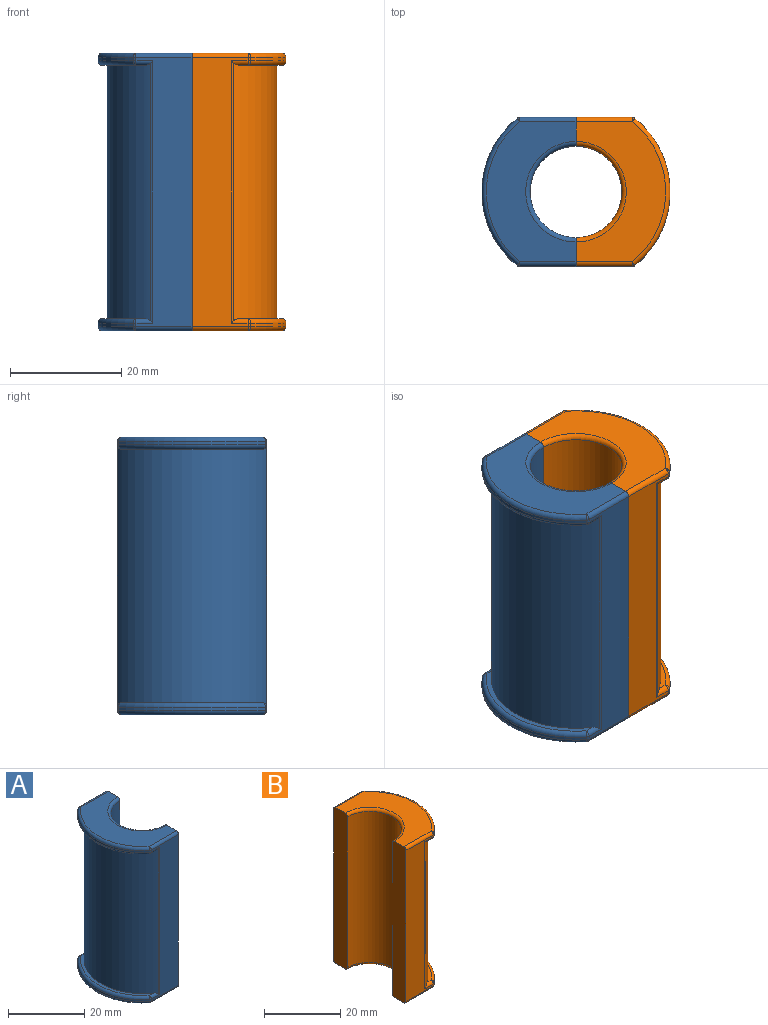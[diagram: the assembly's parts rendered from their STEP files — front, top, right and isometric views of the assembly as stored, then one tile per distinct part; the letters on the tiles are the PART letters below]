
ASSEMBLY  parts=2 mates=1
PART A: 40 faces, bbox 18.3x28.7x50 mm
  f0: plane 50x5.17mm, normal (1,0,0), area 257.8mm2, adj f28,f29,f31,f33,f34,f35,f36,f37
  f1: torus R=16.15mm, axis (0,0,1), area 37.5mm2, adj f3,f8,f9,f10
  f2: torus R=16.15mm, axis (0,0,-1), area 37.5mm2, adj f4,f5,f6,f11
  f3: sphere r=0.8mm, area 0.4mm2, adj f1,f12,f13
  f4: sphere r=0.8mm, area 0.4mm2, adj f2,f15,f16
  f5: sphere r=0.8mm, area 0.4mm2, adj f2,f17,f18
  f6: plane 25.23x7.58mm, normal (0,0,1), area 26.4mm2, adj f2,f7,f15,f18
  f7: cylinder r=15.25mm len=46.42mm, axis (0,0,-1), area 1477mm2, adj f6,f8,f13,f14,f15,f18,f19,f20
  f8: plane 25.23x7.58mm, normal (0,0,-1), area 26.4mm2, adj f1,f7,f13,f20
  f9: sphere r=0.8mm, area 0.4mm2, adj f1,f20,f21
  f10: cylinder r=16.95mm len=26.48mm, axis (0,0,-1), area 18.2mm2, adj f1,f12,f21,f22
  f11: cylinder r=16.95mm len=26.48mm, axis (0,0,1), area 18.2mm2, adj f2,f16,f17,f23
  f12: cylinder r=0.8mm len=0.6mm, axis (0,0,-1), area 0.3mm2, adj f3,f10,f26,f38
  f13: cylinder r=0.8mm len=3.04mm, axis (-1,0,0), area 2.9mm2, adj f3,f7,f8,f14,f38
  f14: cylinder r=0.8mm len=47.2mm, axis (0,0,-1), area 19.1mm2, adj f7,f13,f15,f38
  f15: cylinder r=0.8mm len=3.04mm, axis (-1,0,0), area 2.9mm2, adj f4,f6,f7,f14,f38
  f16: cylinder r=0.8mm len=0.6mm, axis (0,0,1), area 0.3mm2, adj f4,f11,f27,f38
  f17: cylinder r=0.8mm len=0.6mm, axis (0,0,1), area 0.3mm2, adj f5,f11,f25,f37
  f18: cylinder r=0.8mm len=3.04mm, axis (1,0,0), area 2.9mm2, adj f5,f6,f7,f19,f37
  f19: cylinder r=0.8mm len=47.2mm, axis (0,0,-1), area 19.1mm2, adj f7,f18,f20,f37
  f20: cylinder r=0.8mm len=3.04mm, axis (1,0,0), area 2.9mm2, adj f7,f8,f9,f19,f37
  f21: cylinder r=0.8mm len=0.6mm, axis (0,0,-1), area 0.3mm2, adj f9,f10,f24,f37
  f22: torus R=16.15mm, axis (0,0,1), area 37.5mm2, adj f10,f24,f26,f35
  f23: torus R=16.15mm, axis (0,0,-1), area 37.5mm2, adj f11,f25,f27,f31
  f24: sphere r=0.8mm, area 0.4mm2, adj f21,f22,f34
  f25: sphere r=0.8mm, area 0.4mm2, adj f17,f23,f28
  f26: sphere r=0.8mm, area 0.4mm2, adj f12,f22,f32
  f27: sphere r=0.8mm, area 0.4mm2, adj f16,f23,f30
  f28: cylinder r=0.8mm len=10.08mm, axis (-1,0,0), area 12.7mm2, adj f0,f25,f31,f37
  f29: torus R=9.05mm, axis (0,0,-1), area 33.7mm2, adj f0,f31,f36,f39
  f30: cylinder r=0.8mm len=10.08mm, axis (1,0,0), area 12.7mm2, adj f27,f31,f38,f39
  f31: plane 25.23x16.15mm, normal (0,0,-1), area 232.4mm2, adj f0,f23,f28,f29,f30,f39
  f32: cylinder r=0.8mm len=10.08mm, axis (1,0,0), area 12.7mm2, adj f26,f35,f38,f39
  f33: torus R=9.05mm, axis (0,0,1), area 33.7mm2, adj f0,f35,f36,f39
  f34: cylinder r=0.8mm len=10.08mm, axis (-1,0,0), area 12.7mm2, adj f0,f24,f35,f37
  f35: plane 25.23x16.15mm, normal (0,0,1), area 232.4mm2, adj f0,f22,f32,f33,f34,f39
  f36: cylinder r=8.25mm len=48.4mm, axis (0,0,-1), area 1254.4mm2, adj f0,f29,f33,f39
  f37: plane 48.4x10.08mm, normal (0,-1,0), area 344.6mm2, adj f0,f17,f18,f19,f20,f21,f28,f34
  f38: plane 48.4x10.08mm, normal (0,1,0), area 344.6mm2, adj f12,f13,f14,f15,f16,f30,f32,f39
  f39: plane 50x5.17mm, normal (1,0,0), area 257.8mm2, adj f29,f30,f31,f32,f33,f35,f36,f38
PART B: 40 faces, bbox 18.3x28.7x50 mm
  f0: plane 48.4x10.08mm, normal (0,1,0), area 344.6mm2, adj f13,f19,f28,f30,f32,f34,f35,f38
  f1: plane 48.4x10.08mm, normal (0,-1,0), area 344.6mm2, adj f10,f14,f17,f21,f23,f24,f26,f39
  f2: cylinder r=8.25mm len=48.4mm, axis (0,0,-1), area 1254.4mm2, adj f27,f37,f38,f39
  f3: cylinder r=15.25mm len=46.42mm, axis (0,0,-1), area 1477mm2, adj f6,f7,f21,f24,f26,f28,f32,f35
  f4: cylinder r=16.95mm len=26.48mm, axis (0,0,-1), area 18.2mm2, adj f11,f13,f14,f15
  f5: plane 25.23x16.15mm, normal (0,0,1), area 232.4mm2, adj f10,f11,f27,f30,f38,f39
  f6: plane 25.23x7.58mm, normal (0,0,-1), area 26.4mm2, adj f3,f15,f21,f32
  f7: plane 25.23x7.58mm, normal (0,0,1), area 26.4mm2, adj f3,f22,f26,f35
  f8: cylinder r=16.95mm len=26.48mm, axis (0,0,1), area 18.2mm2, adj f16,f19,f22,f23
  f9: plane 25.23x16.15mm, normal (0,0,-1), area 232.4mm2, adj f16,f17,f34,f37,f38,f39
  f10: cylinder r=0.8mm len=10.08mm, axis (-1,0,0), area 12.7mm2, adj f1,f5,f12,f39
  f11: torus R=16.15mm, axis (0,0,1), area 37.5mm2, adj f4,f5,f12,f29
  f12: sphere r=0.8mm, area 0.4mm2, adj f10,f11,f14
  f13: cylinder r=0.8mm len=0.6mm, axis (0,0,-1), area 0.3mm2, adj f0,f4,f29,f31
  f14: cylinder r=0.8mm len=0.6mm, axis (0,0,-1), area 0.3mm2, adj f1,f4,f12,f18
  f15: torus R=16.15mm, axis (0,0,1), area 37.5mm2, adj f4,f6,f18,f31
  f16: torus R=16.15mm, axis (0,0,-1), area 37.5mm2, adj f8,f9,f20,f33
  f17: cylinder r=0.8mm len=10.08mm, axis (-1,0,0), area 12.7mm2, adj f1,f9,f20,f39
  f18: sphere r=0.8mm, area 0.4mm2, adj f14,f15,f21
  f19: cylinder r=0.8mm len=0.6mm, axis (0,0,1), area 0.3mm2, adj f0,f8,f33,f36
  f20: sphere r=0.8mm, area 0.4mm2, adj f16,f17,f23
  f21: cylinder r=0.8mm len=3.04mm, axis (1,0,0), area 2.9mm2, adj f1,f3,f6,f18,f24
  f22: torus R=16.15mm, axis (0,0,-1), area 37.5mm2, adj f7,f8,f25,f36
  f23: cylinder r=0.8mm len=0.6mm, axis (0,0,1), area 0.3mm2, adj f1,f8,f20,f25
  f24: cylinder r=0.8mm len=47.2mm, axis (0,0,-1), area 19.1mm2, adj f1,f3,f21,f26
  f25: sphere r=0.8mm, area 0.4mm2, adj f22,f23,f26
  f26: cylinder r=0.8mm len=3.04mm, axis (1,0,0), area 2.9mm2, adj f1,f3,f7,f24,f25
  f27: torus R=9.05mm, axis (0,0,1), area 33.7mm2, adj f2,f5,f38,f39
  f28: cylinder r=0.8mm len=47.2mm, axis (0,0,-1), area 19.1mm2, adj f0,f3,f32,f35
  f29: sphere r=0.8mm, area 0.4mm2, adj f11,f13,f30
  f30: cylinder r=0.8mm len=10.08mm, axis (1,0,0), area 12.7mm2, adj f0,f5,f29,f38
  f31: sphere r=0.8mm, area 0.4mm2, adj f13,f15,f32
  f32: cylinder r=0.8mm len=3.04mm, axis (-1,0,0), area 2.9mm2, adj f0,f3,f6,f28,f31
  f33: sphere r=0.8mm, area 0.4mm2, adj f16,f19,f34
  f34: cylinder r=0.8mm len=10.08mm, axis (1,0,0), area 12.7mm2, adj f0,f9,f33,f38
  f35: cylinder r=0.8mm len=3.04mm, axis (-1,0,0), area 2.9mm2, adj f0,f3,f7,f28,f36
  f36: sphere r=0.8mm, area 0.4mm2, adj f19,f22,f35
  f37: torus R=9.05mm, axis (0,0,-1), area 33.7mm2, adj f2,f9,f38,f39
  f38: plane 50x5.17mm, normal (-1,0,0), area 257.8mm2, adj f0,f2,f5,f9,f27,f30,f34,f37
  f39: plane 50x5.17mm, normal (-1,0,0), area 257.8mm2, adj f1,f2,f5,f9,f10,f17,f27,f37
PLACE A t=(4,0,0)mm
PLACE B at identity
MATE parallel A.f0 <-> B.f39  axis (1,0,0) through (2,-10.83,25)mm
